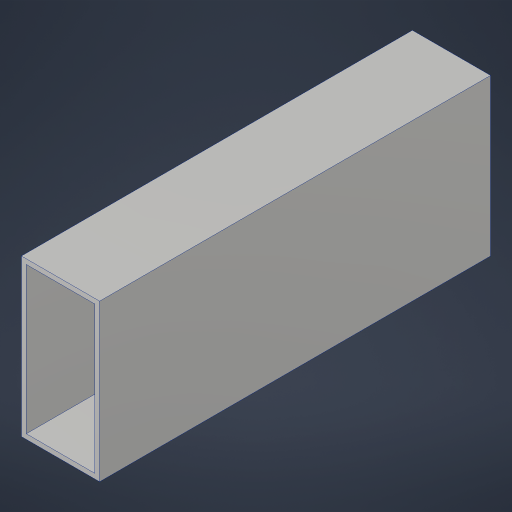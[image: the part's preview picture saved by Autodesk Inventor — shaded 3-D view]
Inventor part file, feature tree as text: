
AUTODESK INVENTOR PART (.ipt)
format: ipt  version: 2023.4 (Build 274418000, 418)  size: 164,864 bytes
history: native  units: in
note: dims shown in document units (in); Inventor stores cm internally (conversion verified against a paired STEP export)
features: extrude x1
ambient origin geometry x8: Origin, YZ Plane, XZ Plane, XY Plane, X Axis, Y Axis, Z Axis, Center Point
bodies: Solid1 (feature_tree)
feature tree (1):
  extrude  "Extrusion1"  TaperAngle=0.0deg  [1 undecoded]
note: 1 required parameter value undecoded (feature->parameter linkage not recoverable at this tier; creation-order binding heuristic only, values carry confidence <= 0.55)
